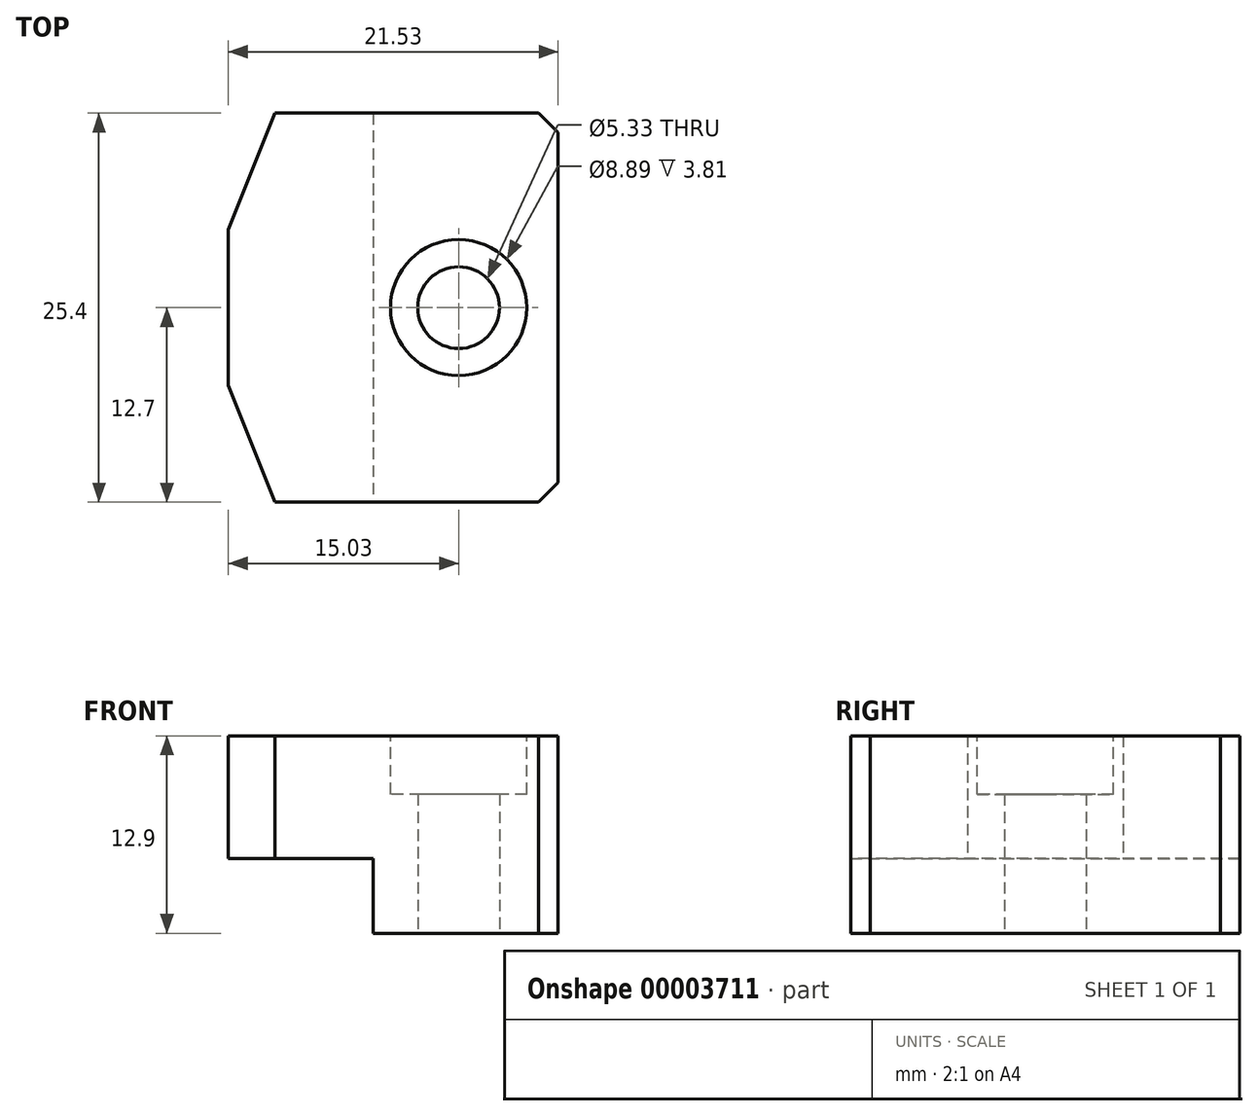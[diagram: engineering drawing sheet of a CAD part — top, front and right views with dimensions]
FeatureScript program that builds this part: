
annotation { "Feature Type Name" : "Feature", "Feature Type Description" : "" }
export const myFeature = defineFeature(function(context is Context, id is Id, definition is map)
    precondition{}
    {
        {
            var Q0;
            Q0=qCreatedBy(makeId("Top.planeOp"),FACE);
            var sketch = newSketch(context, id + "F0", { "sketchPlane" : qUnion([Q0])});
            skLineSegment(sketch, "E0.bottom", {"start": v(0, 25) * mm, "end": v(-140, 25) * mm, "construction": true});
            skLineSegment(sketch, "E0.top", {"start": v(0, -25) * mm, "end": v(-140, -25) * mm, "construction": true});
            skLineSegment(sketch, "E0.left", {"start": v(0, 25) * mm, "end": v(0, -25) * mm, "construction": true});
            skLineSegment(sketch, "E0.right", {"start": v(-140, 25) * mm, "end": v(-140, -25) * mm, "construction": true});
            skArc(sketch, "E1", {"start": v(0, 20) * mm, "mid": v(-10, 0) * mm, "end": v(0, -20) * mm, "construction": true});
            skCircle(sketch, "E2", {"center": v(6.2, 0) * mm, "radius": 2.67 * mm});
            skCircle(sketch, "E3", {"center": v(-146.2, 0) * mm, "radius": 2.67 * mm, "construction": true});
            skLineSegment(sketch, "E4", {"start": v(-146.2, 0) * mm, "end": v(-140, 0) * mm, "construction": true});
            skLineSegment(sketch, "E5", {"start": v(6.2, 0) * mm, "end": v(0, 0) * mm, "construction": true});
            skLineSegment(sketch, "E6", {"start": v(12.7, 11.43) * mm, "end": v(12.7, -11.43) * mm});
            skLineSegment(sketch, "E7", {"start": v(12.7, -11.43) * mm, "end": v(11.43, -12.7) * mm});
            skLineSegment(sketch, "E8", {"start": v(11.43, -12.7) * mm, "end": v(-5.8, -12.7) * mm});
            skLineSegment(sketch, "E9", {"start": v(-5.8, -12.7) * mm, "end": v(-8.83, -5.08) * mm});
            skLineSegment(sketch, "E10", {"start": v(-8.83, -5.08) * mm, "end": v(-8.83, 5.08) * mm});
            skLineSegment(sketch, "E11", {"start": v(-8.83, 5.08) * mm, "end": v(-5.8, 12.7) * mm});
            skLineSegment(sketch, "E12", {"start": v(-5.8, 12.7) * mm, "end": v(11.43, 12.7) * mm});
            skLineSegment(sketch, "E13", {"start": v(11.43, 12.7) * mm, "end": v(12.7, 11.43) * mm});
            skPoint(sketch, "E14", {"position": v(12.7, 0) * mm});
            skPoint(sketch, "E15", {"position": v(-8.83, 0) * mm});
            skSolve(sketch);
        }
        {
            var Q0;
            Q0 = qSketchRegion(id + "F0", true);
            extrude(context, id + "F1", {"entities" : qUnion([Q0]), "depth" : 8 * mm});
        }
        {
            var Q0;
            Q0=makeQuery(id+"F1.opExtrude","CAP_FACE",FACE,{"disambiguationData":[OSD([sQuery(id+"F0.wireOp",EDGE,"E2"),sQuery(id+"F0.wireOp",EDGE,"E6"),sQuery(id+"F0.wireOp",EDGE,"E7"),sQuery(id+"F0.wireOp",EDGE,"E8"),sQuery(id+"F0.wireOp",EDGE,"E9"),sQuery(id+"F0.wireOp",EDGE,"E10"),sQuery(id+"F0.wireOp",EDGE,"E11"),sQuery(id+"F0.wireOp",EDGE,"E12"),sQuery(id+"F0.wireOp",EDGE,"E13")])],"isStart":true});
            var sketch = newSketch(context, id + "F2", { "sketchPlane" : qUnion([Q0])});
            skLineSegment(sketch, "E16", {"start": v(0.64, 12.7) * mm, "end": v(11.43, 12.7) * mm});
            skLineSegment(sketch, "E17", {"start": v(11.43, 12.7) * mm, "end": v(12.7, 11.43) * mm});
            skLineSegment(sketch, "E18", {"start": v(12.7, 11.43) * mm, "end": v(12.7, -11.43) * mm});
            skLineSegment(sketch, "E19", {"start": v(12.7, -11.43) * mm, "end": v(11.43, -12.7) * mm});
            skLineSegment(sketch, "E20", {"start": v(11.43, -12.7) * mm, "end": v(0.64, -12.7) * mm});
            skLineSegment(sketch, "E21", {"start": v(0.64, -12.7) * mm, "end": v(0.64, 12.7) * mm});
            skCircle(sketch, "E22", {"center": v(6.2, 0) * mm, "radius": 2.67 * mm});
            skSolve(sketch);
        }
        {
            var Q0;
            Q0 = qSketchRegion(id + "F2", true);
            extrude(context, id + "F3", {"entities" : qUnion([Q0]), "operationType" : NewBodyOperationType.ADD, "depth" : 4.9 * mm});
        }
        {
            var Q0;
            Q0=makeQuery(id+"F1.opExtrude","CAP_FACE",FACE,{"disambiguationData":[OSD([sQuery(id+"F0.wireOp",EDGE,"E2"),sQuery(id+"F0.wireOp",EDGE,"E6"),sQuery(id+"F0.wireOp",EDGE,"E7"),sQuery(id+"F0.wireOp",EDGE,"E8"),sQuery(id+"F0.wireOp",EDGE,"E9"),sQuery(id+"F0.wireOp",EDGE,"E10"),sQuery(id+"F0.wireOp",EDGE,"E11"),sQuery(id+"F0.wireOp",EDGE,"E12"),sQuery(id+"F0.wireOp",EDGE,"E13")])],"isStart":false});
            var sketch = newSketch(context, id + "F4", { "sketchPlane" : qUnion([Q0])});
            skCircle(sketch, "E23", {"center": v(6.2, 0) * mm, "radius": 4.45 * mm});
            skSolve(sketch);
        }
        {
            var Q0;
            Q0 = qSketchRegion(id + "F4", true);
            extrude(context, id + "F5", {"entities" : qUnion([Q0]), "operationType" : NewBodyOperationType.REMOVE, "oppositeDirection" : true, "depth" : 3.8 * mm});
        }
    });
